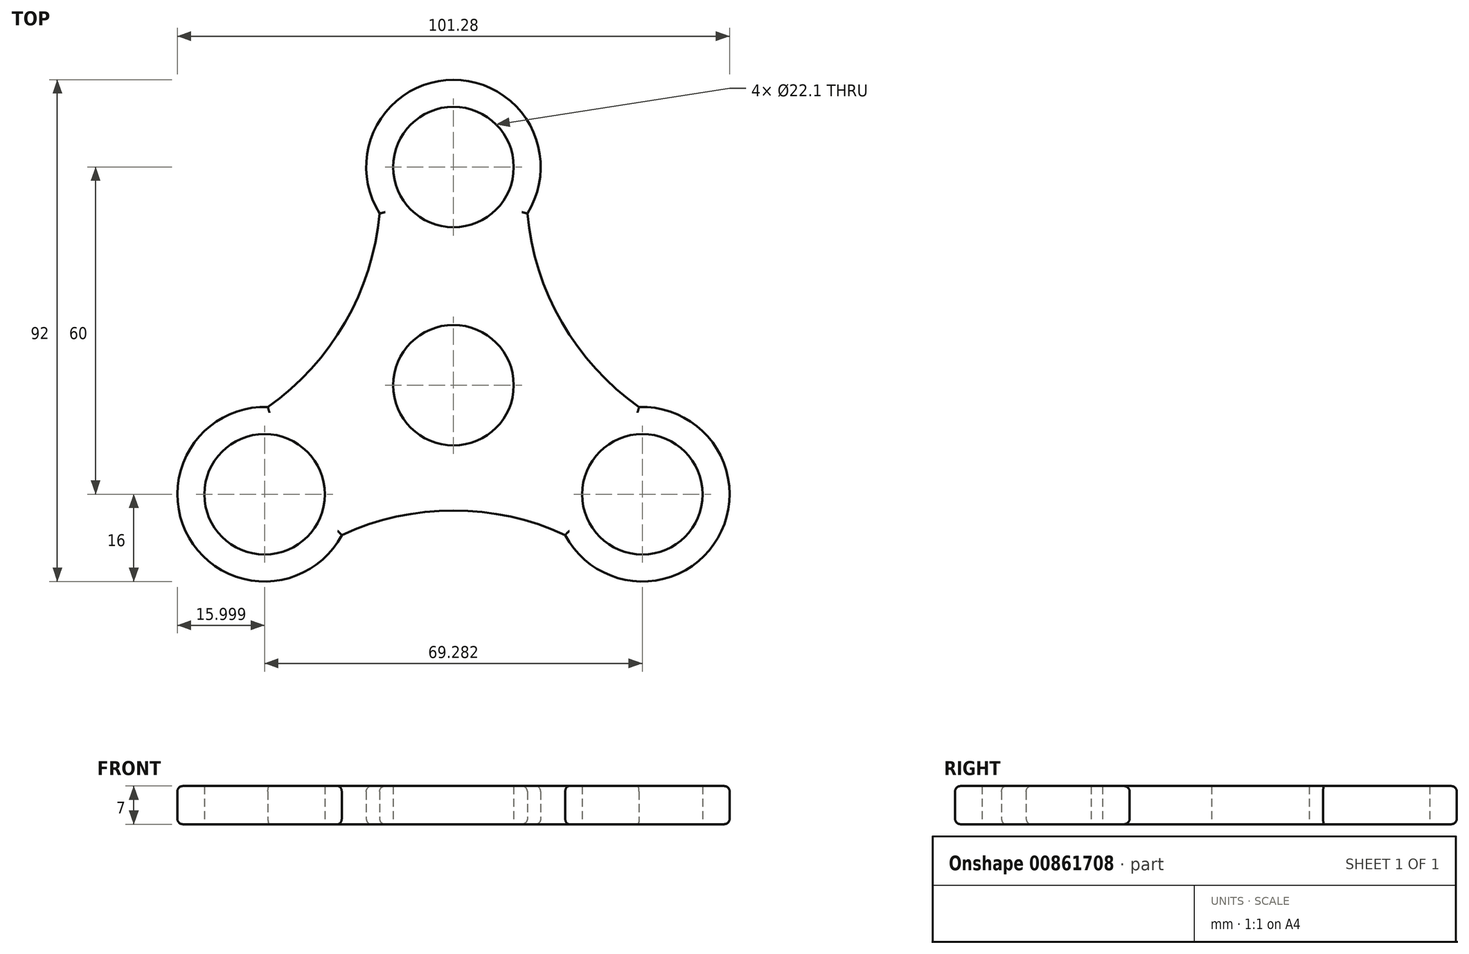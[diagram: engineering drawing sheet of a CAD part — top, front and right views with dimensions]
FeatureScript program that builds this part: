
annotation { "Feature Type Name" : "Feature", "Feature Type Description" : "" }
export const myFeature = defineFeature(function(context is Context, id is Id, definition is map)
    precondition{}
    {
        {
            var Q0;
            Q0=qCreatedBy(makeId("Top.planeOp"),FACE);
            var sketch = newSketch(context, id + "F0", { "sketchPlane" : qUnion([Q0])});
            skCircle(sketch, "E0", {"center": v(0, 0) * mm, "radius": 11.05 * mm});
            skCircle(sketch, "E1", {"center": v(0, 40) * mm, "radius": 11.05 * mm});
            skCircle(sketch, "E2.1.0", {"center": v(-34.64, -20) * mm, "radius": 11.05 * mm});
            skCircle(sketch, "E2.2.0", {"center": v(34.64, -20) * mm, "radius": 11.05 * mm});
            skCircle(sketch, "E3", {"center": v(0, 40) * mm, "radius": 16 * mm});
            skCircle(sketch, "E4.1.0", {"center": v(-34.64, -20) * mm, "radius": 16 * mm});
            skCircle(sketch, "E4.2.0", {"center": v(34.64, -20) * mm, "radius": 16 * mm});
            skLineSegment(sketch, "E5", {"start": v(0, 40) * mm, "end": v(34.64, -20) * mm, "construction": true});
            skLineSegment(sketch, "E6", {"start": v(7.22, 42.45) * mm, "end": v(40.96, -16) * mm, "construction": true});
            skArc(sketch, "E7", {"start": v(13.55, 31.49) * mm, "mid": v(19.89, 11.48) * mm, "end": v(34.04, -4.01) * mm});
            skArc(sketch, "E8.1.0", {"start": v(-34.04, -4.01) * mm, "mid": v(-19.89, 11.48) * mm, "end": v(-13.55, 31.49) * mm});
            skArc(sketch, "E8.2.0", {"start": v(20.5, -27.48) * mm, "mid": v(0, -22.96) * mm, "end": v(-20.5, -27.48) * mm});
            skSolve(sketch);
        }
        {
            var Q0;
            Q0=makeQuery(id+"F0.imprint","IMPRINT",FACE,{"disambiguationData":[TD([[makeQuery(id+"F0.imprint","IMPRINT",EDGE,{"derivedFrom":sQuery(id+"F0.wireOp",EDGE,"E1")}),-1.0]])]});
            var Q1;
            Q1=makeQuery(id+"F0.imprint","IMPRINT",FACE,{"disambiguationData":[TD([[makeQuery(id+"F0.imprint","IMPRINT",EDGE,{"derivedFrom":sQuery(id+"F0.wireOp",EDGE,"E0")}),-1.0]])]});
            var Q2;
            Q2=makeQuery(id+"F0.imprint","IMPRINT",FACE,{"disambiguationData":[TD([[makeQuery(id+"F0.imprint","IMPRINT",EDGE,{"derivedFrom":sQuery(id+"F0.wireOp",EDGE,"E2.1.0")}),-1.0]])]});
            var Q3;
            Q3=makeQuery(id+"F0.imprint","IMPRINT",FACE,{"disambiguationData":[TD([[makeQuery(id+"F0.imprint","IMPRINT",EDGE,{"derivedFrom":sQuery(id+"F0.wireOp",EDGE,"E2.2.0")}),-1.0]])]});
            extrude(context, id + "F1", {"entities" : qUnion([Q0, Q1, Q2, Q3]), "depth" : 7 * mm, "offsetDistance" : 25 * mm});
        }
        {
            var Q0;
            Q0=makeQuery(id+"F1.opExtrude","CAP_EDGE",EDGE,{"disambiguationData":[OSD([sQuery(id+"F0.wireOp",EDGE,"E4.1.0")])],"isStart":false});
            var Q1;
            Q1=makeQuery(id+"F1.opExtrude","CAP_EDGE",EDGE,{"disambiguationData":[OSD([sQuery(id+"F0.wireOp",EDGE,"E8.2.0")])],"isStart":false});
            var Q2;
            Q2=makeQuery(id+"F1.opExtrude","CAP_EDGE",EDGE,{"disambiguationData":[OSD([sQuery(id+"F0.wireOp",EDGE,"E4.2.0")])],"isStart":false});
            var Q3;
            Q3=makeQuery(id+"F1.opExtrude","CAP_EDGE",EDGE,{"disambiguationData":[OSD([sQuery(id+"F0.wireOp",EDGE,"E7")])],"isStart":false});
            var Q4;
            Q4=makeQuery(id+"F1.opExtrude","CAP_EDGE",EDGE,{"disambiguationData":[OSD([sQuery(id+"F0.wireOp",EDGE,"E3")])],"isStart":false});
            var Q5;
            Q5=makeQuery(id+"F1.opExtrude","CAP_EDGE",EDGE,{"disambiguationData":[OSD([sQuery(id+"F0.wireOp",EDGE,"E8.1.0")])],"isStart":false});
            var Q6;
            Q6=makeQuery(id+"F1.opExtrude","CAP_EDGE",EDGE,{"disambiguationData":[OSD([sQuery(id+"F0.wireOp",EDGE,"E8.2.0")])],"isStart":true});
            var Q7;
            Q7=makeQuery(id+"F1.opExtrude","CAP_EDGE",EDGE,{"disambiguationData":[OSD([sQuery(id+"F0.wireOp",EDGE,"E4.1.0")])],"isStart":true});
            var Q8;
            Q8=makeQuery(id+"F1.opExtrude","CAP_EDGE",EDGE,{"disambiguationData":[OSD([sQuery(id+"F0.wireOp",EDGE,"E8.1.0")])],"isStart":true});
            var Q9;
            Q9=makeQuery(id+"F1.opExtrude","CAP_EDGE",EDGE,{"disambiguationData":[OSD([sQuery(id+"F0.wireOp",EDGE,"E3")])],"isStart":true});
            var Q10;
            Q10=makeQuery(id+"F1.opExtrude","CAP_EDGE",EDGE,{"disambiguationData":[OSD([sQuery(id+"F0.wireOp",EDGE,"E7")])],"isStart":true});
            var Q11;
            Q11=makeQuery(id+"F1.opExtrude","CAP_EDGE",EDGE,{"disambiguationData":[OSD([sQuery(id+"F0.wireOp",EDGE,"E4.2.0")])],"isStart":true});
            fillet(context, id + "F2", {"entities" : qUnion([Q0, Q1, Q2, Q3, Q4, Q5, Q6, Q7, Q8, Q9, Q10, Q11]), "radius" : 1 * mm, "tangentPropagation" : true, "allowEdgeOverflow" : false});
        }
    });
